# Revit family: Door_Handle_Generic
name_source: partatom
category: Specialty Equipment
revit_build: Autodesk Revit 2017 (Build: 20160720_1515(x64)
units: mm (PartAtom-declared; Revit-internal decimal feet)

## family parameters
Cut with Voids When Loaded = No
Host = Face
Part Type = Normal
Room Calculation Point = No
Round Connector Dimension = Use Diameter
Shared = Yes

## types (1)
- TL3106SS
    BIMobject Brand = Litto ASSA ABLOY
    BIMobject Product Family = Architectural and Accessory Hardware
    BIMobject Unique ref = TL3106SS
    BIMobject category = Door Hardware
    Date of publishing = 2016-03-04
    Default Elevation = 0 mm  [stored 0 ft]
    Edition number = 1
    Finish = Stainless Steel
    IFC Classification = Door
    NBS Reference Code = 25-38-20-20
    NBS Reference Description = Door Hardware Systems
    OmniClass Code = 23-17 11 11 25
    OmniClass Description = Door Accessories
    Product Group = Architectural and Accessory Hardware
    Product Guid = 10f3c583-c7be-46a9-933c-f754b44adf3e
    Provider = ASSA ABLOY BE
    Uniclass 1.4 Code = L4181
    Uniclass 1.4 Description = Door furniture
    Uniclass 2.0 Code = SS-25-38-20-20
    Uniclass 2.0 Description = Door Hardware Systems

note: [stored X ft] marks values corroborated as IEEE doubles in the binary element streams (Revit-internal decimal feet)

## geometry (parser evidence)
native form markers: Sweep x3
no freeform markers — native parametric forms only
